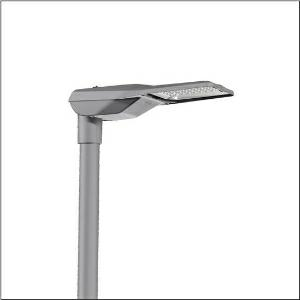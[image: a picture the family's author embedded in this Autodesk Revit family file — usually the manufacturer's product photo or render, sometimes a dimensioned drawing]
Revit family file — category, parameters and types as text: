
# Revit family: streetlight_sl_21_mini___st1_0a_5xe2d33s08hb_eb53
name_source: partatom
category: Lighting Fixtures
units: mm (PartAtom-declared; Revit-internal decimal feet)

## family parameters
Cut with Voids When Loaded = No
Host = Face
Light Source = No
Part Type = Normal
Room Calculation Point = No
Round Connector Dimension = Use Diameter
Shared = No

## types (1)
- --- (1 x LED, 9040 lm, 66 W, 3000K)
    Apparent Load = 66 VA
    CIE Flux Codes = 37 72 97 100 100
    Color Rendering = 70
    Color Temperature = 3000K
    Default Elevation = 1800 mm
    Description = Streetlight SL 21 mini, mast luminaire, primary light control with lens, of PMMA, primary optical cover: cover, of toughened safety glass, transparent, light distribution: ST1.0a, light emission: direct distribution, primary light characteristic: asymmetric, installation type: side-entry, post-top, LED, High Power LED, rated luminous flux: 9.040lm, luminous efficacy: 137lm/W, light colour: 730, colour temperature: 3000K, control gear: D4i, control: flexible luminous flux parameterisation, time-dependent luminous flux control, constant luminous flux control, overheat protection, pre-setting: logarithmic dimming characteristic, mains connection: 220..240V, AC, 50/60Hz, start of lifetime: 66W, end of service life: 69W, reduction: 30W, luminaire housing, of diecast aluminium, powder-coated, Siteco® metallic grey (DB 702S), corrosivity category C5 mid according to DIN EN ISO 12944, please order mast flange separately, inclination adjustable: 0°, 5°, 10°, 15°, sealing non-destructively replaceable, multi-level sealing system, length: 628mm, width: 235mm, height: 110mm, mast flange for spigot size: 42mm (side-entry): 5XC10008XM4, 60/48mm (side-entry/post-top): 5XC10108XM2, 76/60mm (side-entry/post-top): 5XC10108XM1, mounting height: 4..8m, Smart Interface above, protection rating (complete): IP66, insulation class (complete): insulation class II (safety insulation), certification: CE, ENEC, ENEC+, VDE, impact resistance: IK10, permissible operating ambient temperature for outdoor applications: -40..+50°C, standard-compliant lighting for roads and squares, packaging unit: 1 piece

Light Distribution: ST1.0a
    Height = 110 mm
    Lamp = 1 x LED
    Lamp Light Flux = 9040 lm
    Lamp Power = 66 W
    Lamp count = 1
    Length = 625 mm
    Luminous efficacy = 137 lm/W
    Manufacturer = Siteco
    ModVariant = No
    Model = 5XE2D33S08HB
    Number of Poles = 1
    OnlyDefault = Yes
    Power Factor = 1
    Product Name = Streetlight SL 21 mini | ST1.0a
    Product group = mast luminaire | pylon top
    ProductGroupID = 6100
    Protection Class = Protection class II
    Protection Degree = IP 66
    RLX_Detail_Level = 1
    RLX_Emergency_Light_Flux = 0 lm
    RLX_Emergency_Type = 0
    RLX_Emergency_Type_DB = No
    RlxData = <blob elided: 26169 chars, md5=a031afd2>
    Socket = socket
    Standby Power = 0 W
    System Light Flux = 9040 lm
    System Power = 66 W
    Type Comments = factory setting: luminous flux: 100 % | dim-lin: 254 | 670 mA
    Type Image = l_1003515.jpg
    URL = http://relux.com
    VarID = @adj_209955
    Voltage = 0 V
    Weight = 0.00 kg
    Width = 234 mm

## geometry (parser evidence)
native form markers: Blend x4, Sweep x12
no freeform markers — native parametric forms only
